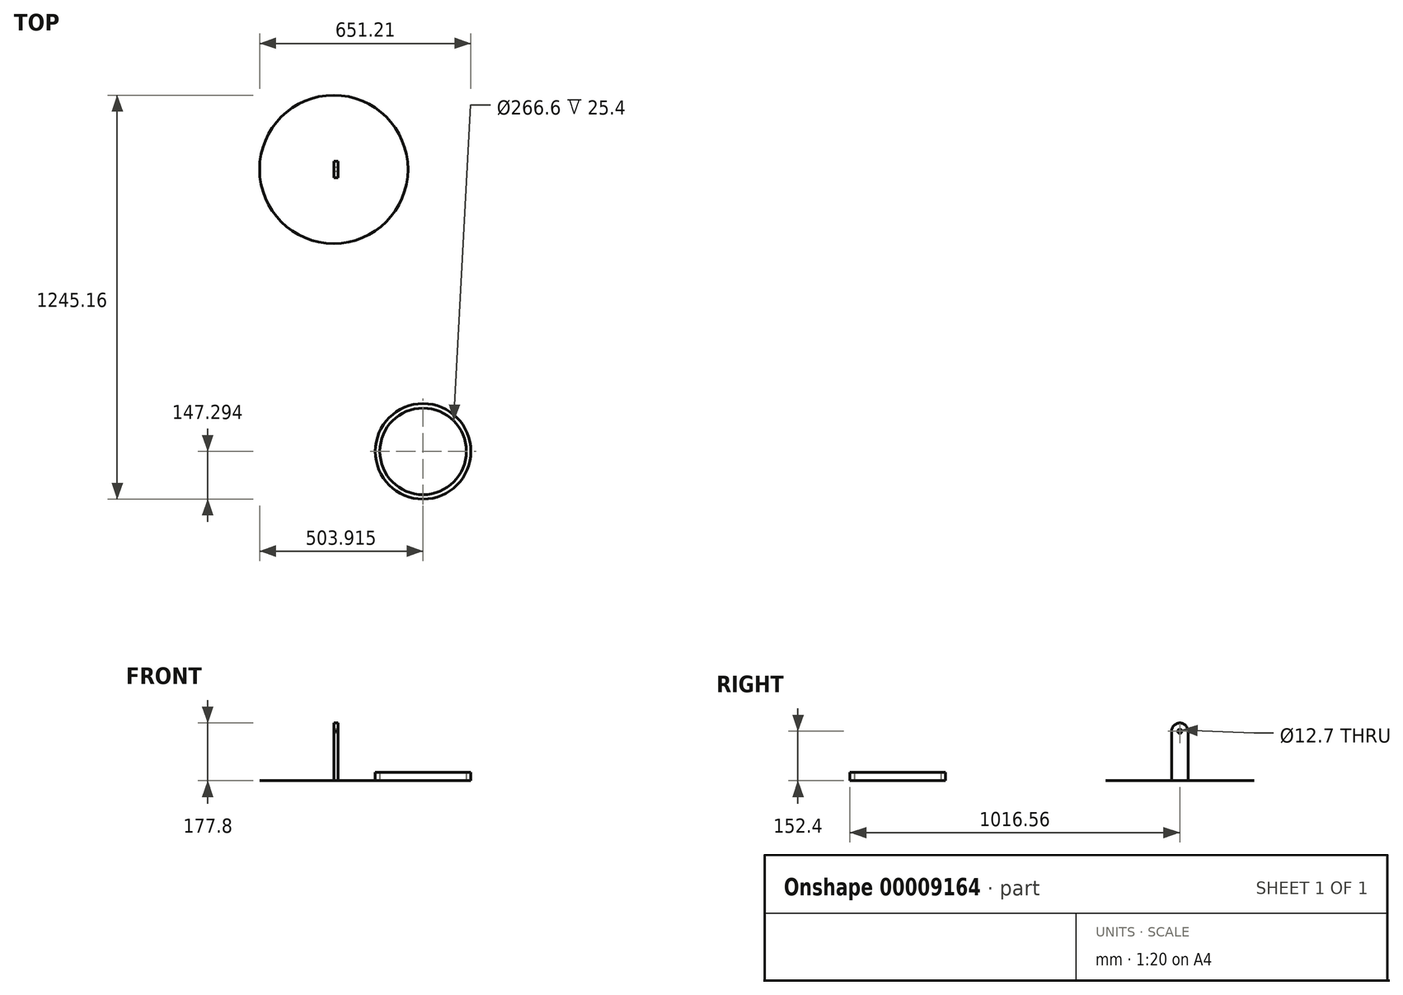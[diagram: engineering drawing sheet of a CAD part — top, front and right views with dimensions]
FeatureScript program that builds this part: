
annotation { "Feature Type Name" : "Feature", "Feature Type Description" : "" }
export const myFeature = defineFeature(function(context is Context, id is Id, definition is map)
    precondition{}
    {
        {
            var Q0;
            Q0=qCreatedBy(makeId("Right.planeOp"),FACE);
            var sketch = newSketch(context, id + "F0", { "sketchPlane" : qUnion([Q0])});
            skArc(sketch, "E0", {"start": v(25.4, 152.4) * mm, "mid": v(-0.38, 177.8) * mm, "end": v(-25.39, 151.64) * mm});
            skLineSegment(sketch, "E1", {"start": v(-25.39, 153.16) * mm, "end": v(-25.39, 0) * mm});
            skLineSegment(sketch, "E2", {"start": v(-25.39, 0) * mm, "end": v(25.4, 0) * mm});
            skLineSegment(sketch, "E3", {"start": v(25.4, 0) * mm, "end": v(25.4, 152.4) * mm});
            skCircle(sketch, "E4", {"center": v(0, 152.4) * mm, "radius": 6.35 * mm});
            skSolve(sketch);
        }
        {
            var Q0;
            Q0=qCreatedBy(makeId("Top.planeOp"),FACE);
            var sketch = newSketch(context, id + "F1", { "sketchPlane" : qUnion([Q0])});
            skCircle(sketch, "E5", {"center": v(0, 0) * mm, "radius": 228.6 * mm});
            skSolve(sketch);
        }
        {
            var Q0;
            Q0=makeQuery(id+"F1.imprint","IMPRINT",FACE,{"disambiguationData":[TD([[makeQuery(id+"F1.imprint","IMPRINT",EDGE,{"derivedFrom":sQuery(id+"F1.wireOp",EDGE,"E5")}),1.0]])]});
            extrude(context, id + "F2", {"entities" : qUnion([Q0]), "depth" : 1 / 203.2 * mm});
        }
        {
            var Q0;
            {var subQ1=sQuery(id+"F0.wireOp",EDGE,"E2");Q0=makeQuery(id+"F0.imprint","IMPRINT",FACE,{"disambiguationData":[TD([[makeQuery(id+"F0.imprint","IMPRINT",EDGE,{"derivedFrom":subQ1}),1.0]])]});}
            extrude(context, id + "F3", {"entities" : qUnion([Q0]), "depth" : 12.7 * mm});
        }
        {
            var Q0;
            Q0=qCreatedBy(makeId("Top.planeOp"),FACE);
            var sketch = newSketch(context, id + "F4", { "sketchPlane" : qUnion([Q0])});
            skCircle(sketch, "E6", {"center": v(275.31, -869.27) * mm, "radius": 147.3 * mm});
            skCircle(sketch, "E7", {"center": v(275.31, -869.27) * mm, "radius": 133.3 * mm});
            skSolve(sketch);
        }
        {
            var Q0;
            Q0=makeQuery(id+"F4.imprint","IMPRINT",FACE,{"disambiguationData":[TD([[makeQuery(id+"F4.imprint","IMPRINT",EDGE,{"derivedFrom":sQuery(id+"F4.wireOp",EDGE,"E6")}),1.0]])]});
            extrude(context, id + "F5", {"entities" : qUnion([Q0]), "depth" : 25.4 * mm});
        }
    });
